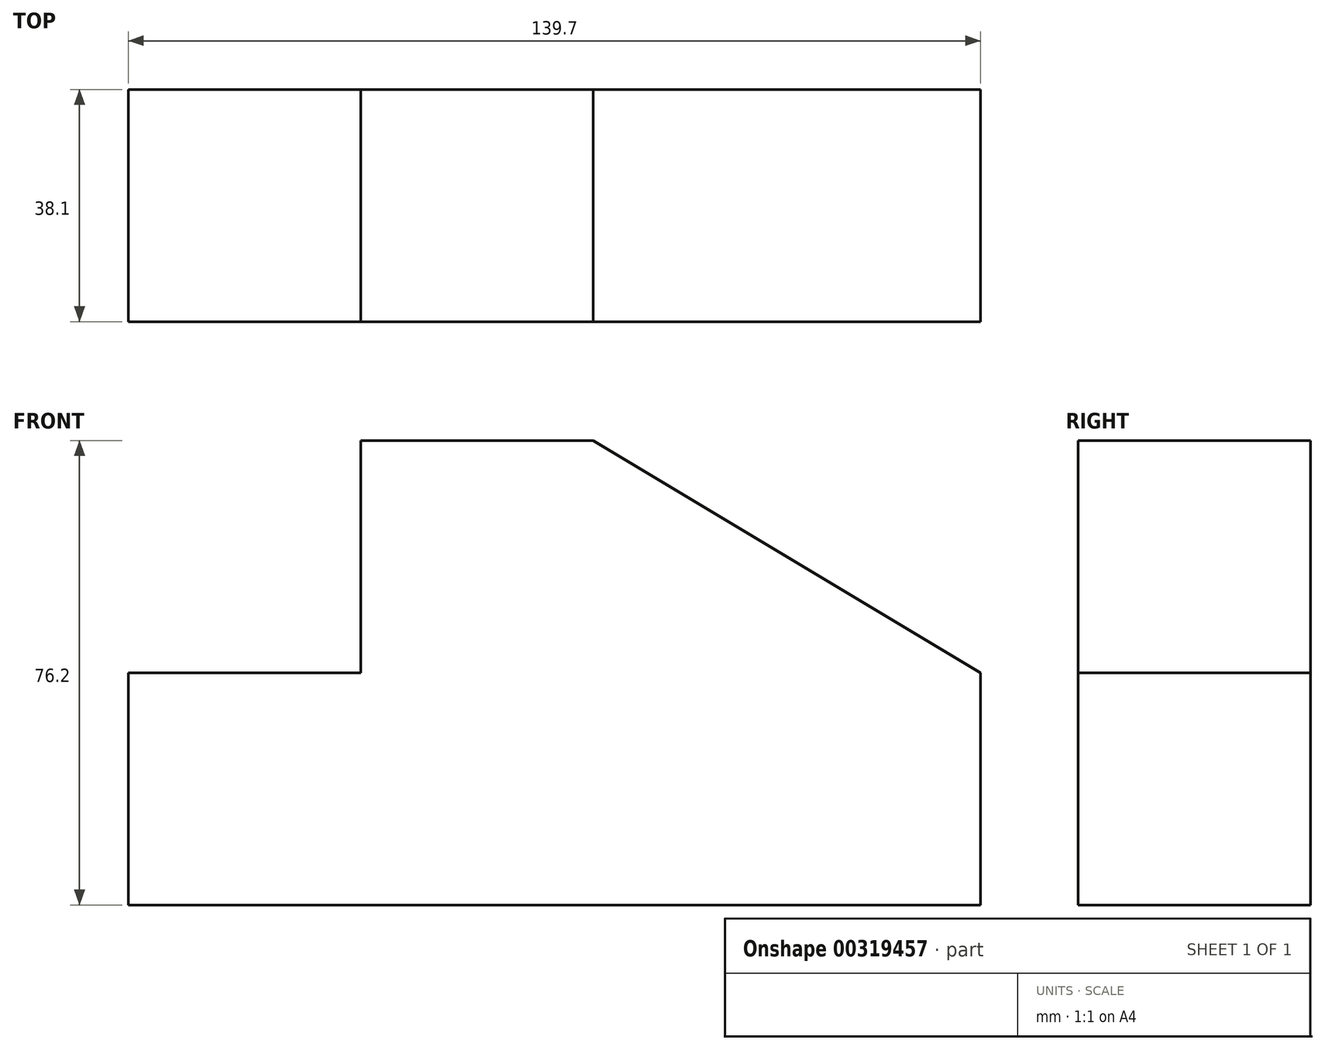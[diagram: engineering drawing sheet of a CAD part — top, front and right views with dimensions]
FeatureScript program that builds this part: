
annotation { "Feature Type Name" : "Feature", "Feature Type Description" : "" }
export const myFeature = defineFeature(function(context is Context, id is Id, definition is map)
    precondition{}
    {
        {
            var Q0;
            Q0=qCreatedBy(makeId("Front.planeOp"),FACE);
            var sketch = newSketch(context, id + "F0", { "sketchPlane" : qUnion([Q0])});
            skLineSegment(sketch, "E0", {"start": v(-78.64, -31.97) * mm, "end": v(61.06, -31.97) * mm});
            skLineSegment(sketch, "E1", {"start": v(61.06, 6.13) * mm, "end": v(61.06, -31.97) * mm});
            skLineSegment(sketch, "E2", {"start": v(61.06, 6.13) * mm, "end": v(-2.44, 44.23) * mm});
            skLineSegment(sketch, "E3", {"start": v(-2.44, 44.23) * mm, "end": v(-40.54, 44.23) * mm});
            skLineSegment(sketch, "E4", {"start": v(-40.54, 44.23) * mm, "end": v(-40.54, 6.13) * mm});
            skLineSegment(sketch, "E5", {"start": v(-40.54, 6.13) * mm, "end": v(-78.64, 6.13) * mm});
            skLineSegment(sketch, "E6", {"start": v(-78.64, 6.13) * mm, "end": v(-78.64, -31.97) * mm});
            skSolve(sketch);
        }
        {
            var Q0;
            Q0=makeQuery(id+"F0.imprint","IMPRINT",FACE,{"disambiguationData":[TD([[makeQuery(id+"F0.imprint","IMPRINT",EDGE,{"derivedFrom":sQuery(id+"F0.wireOp",EDGE,"E0")}),1.0]])]});
            extrude(context, id + "F1", {"entities" : qUnion([Q0]), "depth" : 38.1 * mm});
        }
    });
